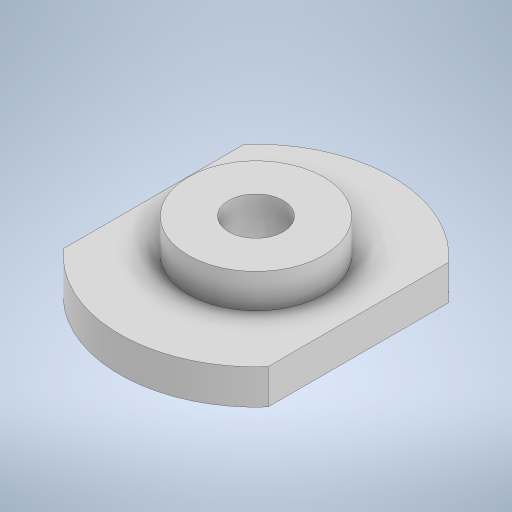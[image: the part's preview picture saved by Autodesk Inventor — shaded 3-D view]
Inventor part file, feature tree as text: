
AUTODESK INVENTOR PART (.ipt)
format: ipt  version: 2024 (Build 280153020, 153B)  size: 255,488 bytes
history: native  units: mm
features: extrude x4, sketch x3, mirror x1, projected_geometry x1
ambient origin geometry x8: Origin, YZ Plane, XZ Plane, XY Plane, X Axis, Y Axis, Z Axis, Center Point
bodies: Solid1 (feature_tree)
feature tree (9):
  sketch  "Sketch1"  dims[d0=7.95mm d1=3.2mm]
  extrude  "Extrusion1"  Depth=3.2mm
  extrude  "Extrusion2"  Depth=2.0mm TaperAngle=0.0deg
  extrude  "Extrusion4"  Depth=2.0mm
  mirror  "Mirror1"
  extrude  "Extrusion5"  Depth=2.0mm TaperAngle=0.0deg
  sketch  "Sketch3"  dims[d2=16.0mm d3=2.0mm d4=0.0mm]
  sketch  "Sketch4"  dims[d5=3.8mm d6=0.0mm d11=2.0mm d13=6.75mm d14=0.0mm d15=1.75mm d16=0.0mm]
  projected_geometry  "Projected Loop1"
